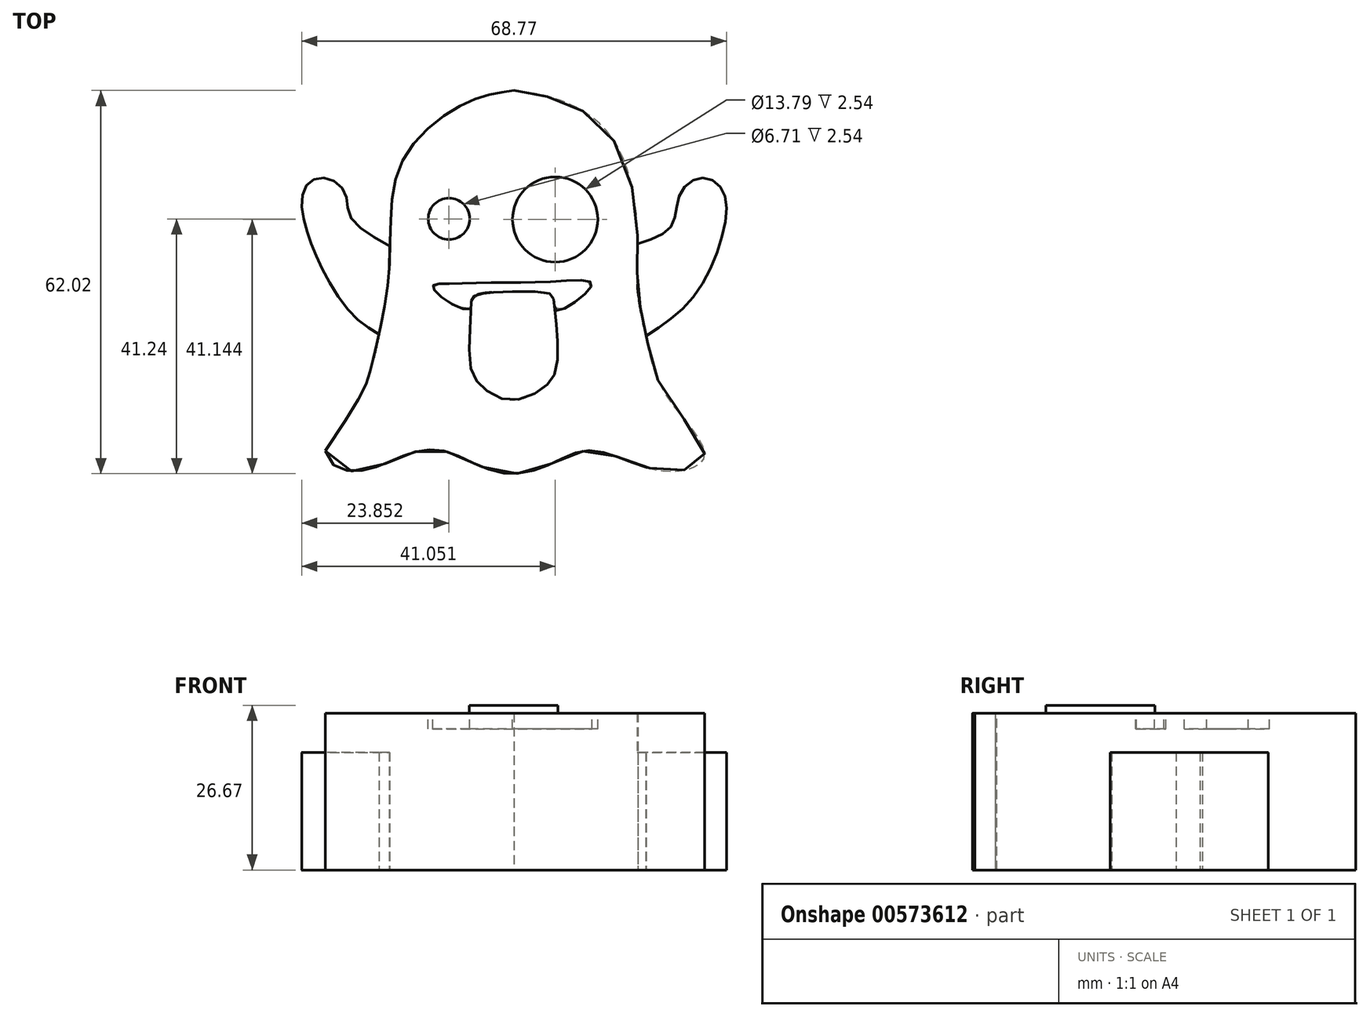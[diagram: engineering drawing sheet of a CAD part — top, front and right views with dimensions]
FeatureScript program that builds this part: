
annotation { "Feature Type Name" : "Feature", "Feature Type Description" : "" }
export const myFeature = defineFeature(function(context is Context, id is Id, definition is map)
    precondition{}
    {
        {
            var Q0;
            Q0=qCreatedBy(makeId("Top.planeOp"),FACE);
            var sketch = newSketch(context, id + "F0", { "sketchPlane" : qUnion([Q0])});
            skFitSpline(sketch, "E0", {"points": [v(0, 33.37) * mm, v(-7.03, 31.69) * mm, v(-18.14, 21.85) * mm, v(-20.2, 4.64) * mm, v(-22.78, -10) * mm, v(-30.58, -24.95) * mm], "startDerivative": vector(-46.08, -6.92) * mm, "endDerivative": vector(-91.46, -132.61) * mm});
            skFitSpline(sketch, "E1", {"points": [v(-30.58, -24.95) * mm, v(-24.72, -28.16) * mm, v(-17.9, -25.74) * mm, v(-11.49, -24.95) * mm, v(-3.25, -28.24) * mm, v(4.42, -27.74) * mm, v(11.56, -24.95) * mm, v(18.87, -26.78) * mm, v(26.52, -28.24) * mm, v(30.85, -25.7) * mm, v(24.56, -15.85) * mm, v(21.42, -6.6) * mm, v(19.97, 1.7) * mm, v(19.99, 10.33) * mm, v(16.2, 25.2) * mm, v(7.47, 31.76) * mm, v(0, 33.37) * mm], "startDerivative": vector(37.88, -163.37) * mm, "endDerivative": vector(-123.08, 14.96) * mm});
            skSolve(sketch);
        }
        {
            var Q0;
            Q0=qCreatedBy(makeId("Top.planeOp"),FACE);
            var sketch = newSketch(context, id + "F1", { "sketchPlane" : qUnion([Q0])});
            skFitSpline(sketch, "E2", {"points": [v(-21.85, -6.15) * mm, v(-26.36, -2.74) * mm, v(-31.05, 4.47) * mm, v(-33.33, 9.93) * mm, v(-34.41, 15.22) * mm, v(-33.1, 18.55) * mm, v(-30.03, 19.1) * mm, v(-27.33, 16.69) * mm, v(-26.58, 13.03) * mm, v(-20.15, 8.18) * mm], "startDerivative": vector(-39.33, 23.82) * mm, "endDerivative": vector(59.82, -33.24) * mm});
            skFitSpline(sketch, "E3", {"points": [v(19.95, 8.53) * mm, v(25.55, 11.56) * mm, v(26.72, 16.3) * mm, v(30.11, 19.2) * mm, v(33.6, 17.45) * mm, v(33.92, 10.81) * mm, v(29.03, 0) * mm, v(21.4, -6.39) * mm], "startDerivative": vector(50, 16.36) * mm, "endDerivative": vector(-46.71, -30.92) * mm});
            skFitSpline(sketch, "E4", {"points": [v(-20.15, 8.18) * mm, v(-20.72, -2.19) * mm, v(-21.85, -6.15) * mm], "startDerivative": vector(-0.33, -18.94) * mm, "endDerivative": vector(-3.29, -8.96) * mm});
            skFitSpline(sketch, "E5", {"points": [v(21.4, -6.39) * mm, v(19.95, 0.9) * mm, v(19.95, 8.53) * mm], "startDerivative": vector(-3.63, 14.56) * mm, "endDerivative": vector(0.73, 15.28) * mm});
            skSolve(sketch);
        }
        {
            var Q0;
            Q0=makeQuery(id+"F0.imprint","IMPRINT",FACE,{"disambiguationData":[TD([[makeQuery(id+"F0.imprint","IMPRINT",EDGE,{"derivedFrom":sQuery(id+"F0.wireOp",EDGE,"E0")}),1.0]])]});
            extrude(context, id + "F2", {"entities" : qUnion([Q0]), "depth" : 25.4 * mm, "offsetDistance" : 25.4 * mm});
        }
        {
            var Q0;
            Q0=makeQuery(id+"F1.imprint","IMPRINT",FACE,{"disambiguationData":[TD([[makeQuery(id+"F1.imprint","IMPRINT",EDGE,{"derivedFrom":sQuery(id+"F1.wireOp",EDGE,"E2")}),-1.0]])]});
            var Q1;
            Q1=makeQuery(id+"F1.imprint","IMPRINT",FACE,{"disambiguationData":[TD([[makeQuery(id+"F1.imprint","IMPRINT",EDGE,{"derivedFrom":sQuery(id+"F1.wireOp",EDGE,"E3")}),-1.0]])]});
            extrude(context, id + "F3", {"entities" : qUnion([Q0, Q1]), "operationType" : NewBodyOperationType.ADD, "depth" : 19.05 * mm, "offsetDistance" : 25.4 * mm});
        }
        {
            var Q0;
            Q0=makeQuery(id+"F2.opExtrude","CAP_FACE",FACE,{"disambiguationData":[OSD([sQuery(id+"F0.wireOp",EDGE,"E0"),sQuery(id+"F0.wireOp",EDGE,"E1")])],"isStart":false});
            cPlane(context, id + "F4", {"entities" : qUnion([Q0]), "cplaneType" : CPlaneType.OFFSET, "offset" : 0 * mm, "width" : 152.4 * mm, "height" : 152.4 * mm});
        }
        {
            var Q0;
            Q0=qCreatedBy(id+"F4.planeOp",FACE);
            var sketch = newSketch(context, id + "F5", { "sketchPlane" : qUnion([Q0])});
            skCircle(sketch, "E6", {"center": v(-10.56, 12.59) * mm, "radius": 3.36 * mm});
            skPoint(sketch, "E6.first.point", {"position": v(-10.47, 15.95) * mm});
            skPoint(sketch, "E6.second.point", {"position": v(-7.24, 12.05) * mm});
            skPoint(sketch, "E6.third.point", {"position": v(-13.31, 10.67) * mm});
            skCircle(sketch, "E7", {"center": v(6.64, 12.5) * mm, "radius": 6.9 * mm});
            skPoint(sketch, "E7.first.point", {"position": v(8.05, 19.25) * mm});
            skPoint(sketch, "E7.second.point", {"position": v(9.72, 6.32) * mm});
            skPoint(sketch, "E7.third.point", {"position": v(2.14, 7.27) * mm});
            skFitSpline(sketch, "E8", {"points": [v(-7.1, -1.98) * mm, v(-11.22, -0.48) * mm, v(-13.15, 1.73) * mm, v(-11.05, 2.08) * mm, v(-2.94, 2.3) * mm, v(6.38, 2.43) * mm, v(12.54, 2.23) * mm, v(10.16, -0.65) * mm, v(6.74, -2.14) * mm, v(6.37, -0.27) * mm, v(4.87, 0.67) * mm, v(-1.12, 0.7) * mm, v(-5.2, 0.53) * mm, v(-6.82, -0.43) * mm, v(-7.1, -1.98) * mm]});
            skSolve(sketch);
        }
        {
            var Q0;
            Q0=makeQuery(id+"F5.imprint","IMPRINT",FACE,{"disambiguationData":[TD([[makeQuery(id+"F5.imprint","IMPRINT",EDGE,{"derivedFrom":sQuery(id+"F5.wireOp",EDGE,"E8")}),-1.0]])]});
            var Q1;
            Q1=makeQuery(id+"F5.imprint","IMPRINT",FACE,{"disambiguationData":[TD([[makeQuery(id+"F5.imprint","IMPRINT",EDGE,{"derivedFrom":sQuery(id+"F5.wireOp",EDGE,"E6")}),1.0]])]});
            var Q2;
            Q2=makeQuery(id+"F5.imprint","IMPRINT",FACE,{"disambiguationData":[TD([[makeQuery(id+"F5.imprint","IMPRINT",EDGE,{"derivedFrom":sQuery(id+"F5.wireOp",EDGE,"E7")}),1.0]])]});
            extrude(context, id + "F6", {"entities" : qUnion([Q0, Q1, Q2]), "operationType" : NewBodyOperationType.REMOVE, "oppositeDirection" : true, "depth" : 2.54 * mm, "offsetDistance" : 25.4 * mm});
        }
        {
            var Q0;
            Q0=qCreatedBy(id+"F4.planeOp",FACE);
            var sketch = newSketch(context, id + "F7", { "sketchPlane" : qUnion([Q0])});
            skFitSpline(sketch, "E9", {"points": [v(-6.94, -0.73) * mm, v(-7.05, -3.68) * mm, v(-7.05, -11.45) * mm, v(-5.12, -14.66) * mm, v(-0.42, -16.77) * mm, v(4.76, -14.74) * mm, v(6.66, -12.2) * mm, v(7, -6.3) * mm, v(6.52, -1.68) * mm, v(6.3, 0) * mm, v(5.1, 0.7) * mm, v(-2.98, 0.72) * mm, v(-5.26, 0.47) * mm, v(-6.66, 0) * mm, v(-6.94, -0.73) * mm]});
            skSolve(sketch);
        }
        {
            var Q0;
            Q0=makeQuery(id+"F7.imprint","IMPRINT",FACE,{"disambiguationData":[TD([[makeQuery(id+"F7.imprint","IMPRINT",EDGE,{"derivedFrom":sQuery(id+"F7.wireOp",EDGE,"E9")}),1.0]])]});
            extrude(context, id + "F8", {"entities" : qUnion([Q0]), "operationType" : NewBodyOperationType.ADD, "depth" : 1.27 * mm, "offsetDistance" : 25.4 * mm});
        }
    });
